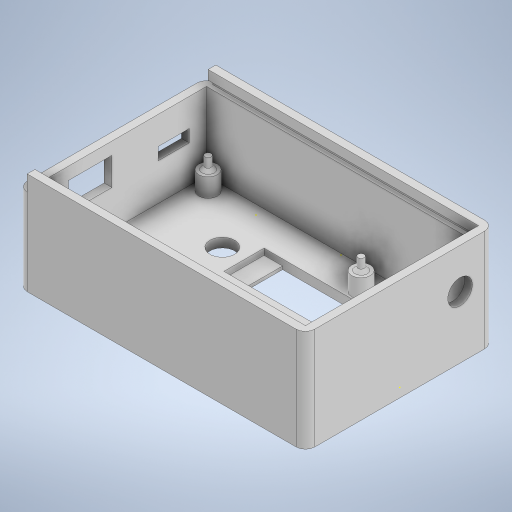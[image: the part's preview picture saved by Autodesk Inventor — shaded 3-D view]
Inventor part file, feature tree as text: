
AUTODESK INVENTOR PART (.ipt)
format: ipt  version: 2024.2 (Build 282272000, 272)  size: 510,464 bytes
history: native  units: mm
features: sketch x27, extrude x21, other x14, chamfer x1, mirror x1
ambient origin geometry x8: Origin, YZ Plane, XZ Plane, XY Plane, X Axis, Y Axis, Z Axis, Center Point
bodies: Body1 (feature_tree)
feature tree (64):
  other  "Поперечное сечение1"
  other  "Поперечное сечение2"
  other  "Поперечное сечение3"
  other  "Поперечное сечение4"
  other  "Поперечное сечение5"
  other  "Поперечное сечение6"
  other  "Поперечное сечение7"
  other  "Поперечное сечение8"
  other  "Поперечное сечение9"
  other  "Поперечное сечение10"
  other  "Поперечное сечение11"
  other  "Поперечное сечение12"
  other  "Поперечное сечение13"
  other  "Твердое тело1"
  extrude  "Выдавливание1"  Depth=87.0mm
  extrude  "Выдавливание2"  Depth=55.0mm
  extrude  "Выдавливание3"  Depth=6.0mm
  extrude  "Выдавливание4"  Depth=6.0mm
  extrude  "Выдавливание5"  Depth=6.0mm
  sketch  "Эскиз6"
  extrude  "Выдавливание6"  Depth=6.0mm
  extrude  "Выдавливание7"  Depth=25.0mm TaperAngle=0.0deg
  chamfer  "Фаска1"  Distance=3.0mm
  sketch  "Эскиз9"
  sketch  "Эскиз10"
  extrude  "Выдавливание8"  Depth=8.0mm
  extrude  "Выдавливание9"  Depth=86.25mm TaperAngle=0.0deg
  sketch  "Эскиз13"
  extrude  "Выдавливание10"  Depth=7.0mm
  extrude  "Выдавливание11"  Depth=38.0mm
  mirror  "Зеркальное отражение1"
  extrude  "Выдавливание12"  Depth=6.0mm
  extrude  "Выдавливание13"  Depth=27.0mm
  extrude  "Выдавливание14"  Depth=12.0mm
  sketch  "Эскиз19"
  extrude  "Выдавливание15"  Depth=2.0mm TaperAngle=0.0deg
  extrude  "Выдавливание16"  Depth=3.0mm TaperAngle=0.0deg
  extrude  "Выдавливание17"  Depth=4.0mm
  sketch  "Эскиз23"
  extrude  "Выдавливание18"  Depth=3.5mm
  extrude  "Выдавливание19"  Depth=6.0mm
  extrude  "Выдавливание20"  Depth=4.0mm
  extrude  "Выдавливание21"  Depth=4.5mm
  sketch  "Эскиз1"
  sketch  "Эскиз2"
  sketch  "Эскиз3"
  sketch  "Эскиз4"
  sketch  "Эскиз5"
  sketch  "Эскиз7"
  sketch  "Эскиз8"
  sketch  "Эскиз11"
  sketch  "Эскиз12"
  sketch  "Эскиз14"
  sketch  "Эскиз15"
  sketch  "Эскиз16"
  sketch  "Эскиз17"
  sketch  "Эскиз18"
  sketch  "Эскиз20"
  sketch  "Эскиз21"
  sketch  "Эскиз22"
  sketch  "Эскиз24"
  sketch  "Эскиз25"
  sketch  "Эскиз26"
  sketch  "Эскиз27"
